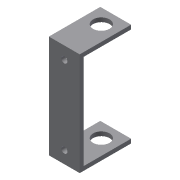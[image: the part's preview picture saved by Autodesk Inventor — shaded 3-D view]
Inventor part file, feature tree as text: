
AUTODESK INVENTOR PART (.ipt)
format: ipt  version: 2015 (Build 190159000, 159)  size: 104,960 bytes
history: native  units: mm
features: extrude x3, sketch x2
ambient origin geometry x8: Origin, YZ Plane, XZ Plane, XY Plane, X Axis, Y Axis, Z Axis, Center Point
bodies: Solid1 (feature_tree)
feature tree (5):
  sketch  "Sketch1"  dims[d0=15.0mm d1=50.0mm]
  extrude  "Extrusion1"  Depth=50.0mm
  extrude  "Extrusion2"  Depth=50.0mm
  extrude  "Extrusion3"  Depth=50.0mm
  sketch  "Sketch2"  dims[d2=1.0mm d3=38.0mm d4=3.0mm d5=3.0mm d6=15.0mm d7=2.0mm d8=15.0mm d9=2.0mm d10=2.0mm d11=0.0mm d12=25.0mm d13=0.0mm d14=18.0mm d15=90.0deg d16=8.0mm d17=50.0mm d18=0.0mm]
